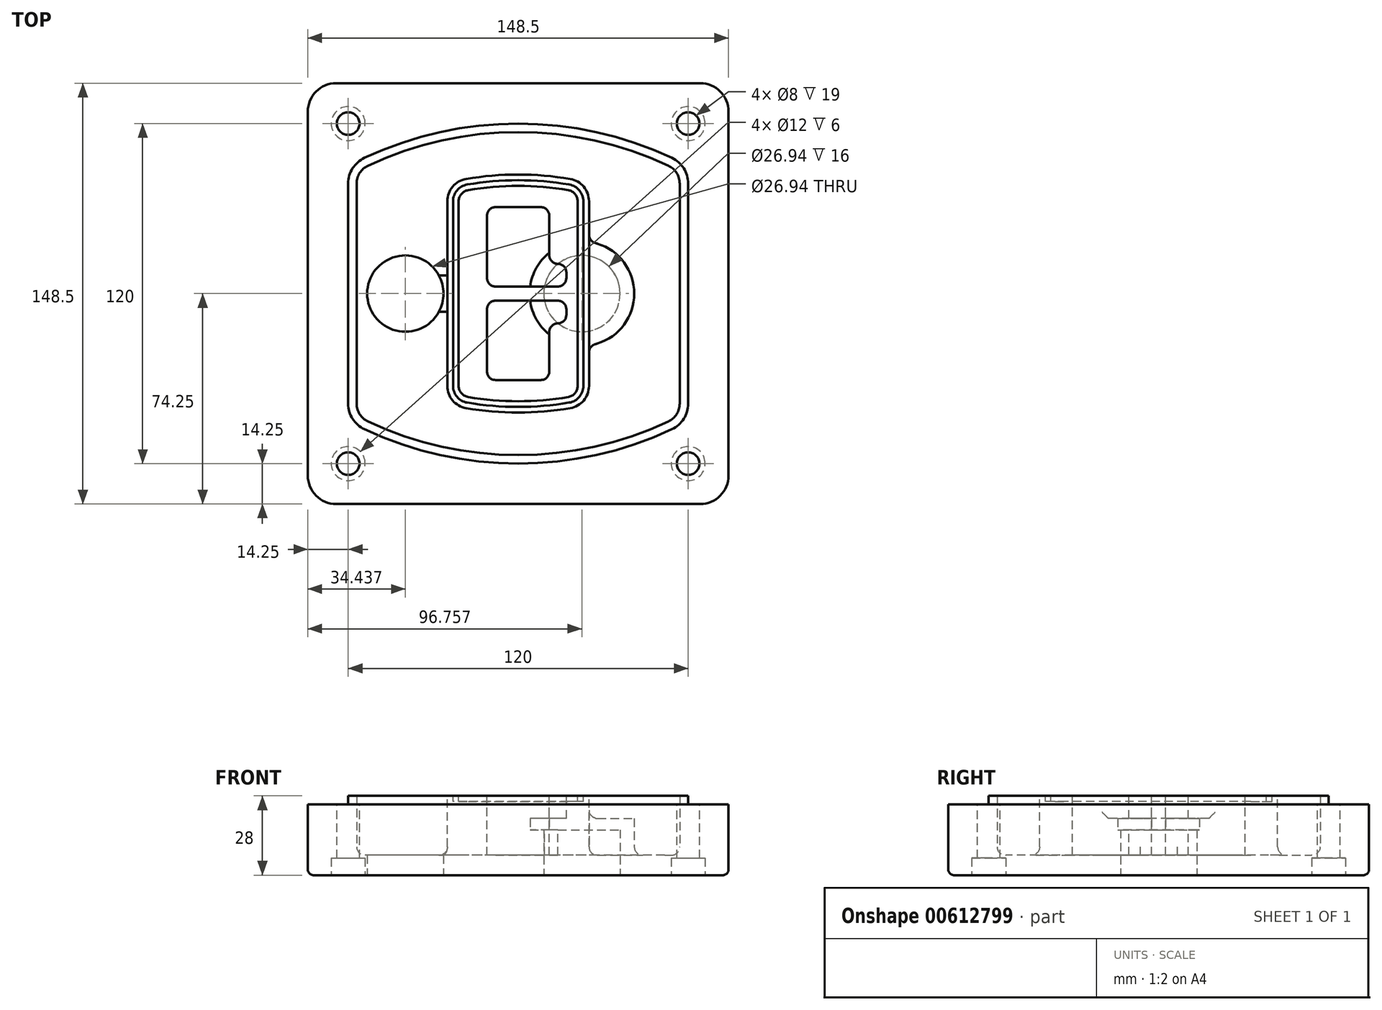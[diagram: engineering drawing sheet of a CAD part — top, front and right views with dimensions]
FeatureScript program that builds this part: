
annotation { "Feature Type Name" : "Feature", "Feature Type Description" : "" }
export const myFeature = defineFeature(function(context is Context, id is Id, definition is map)
    precondition{}
    {
        {
            var Q0;
            Q0=qCreatedBy(makeId("Top.planeOp"),FACE);
            var sketch = newSketch(context, id + "F0", { "sketchPlane" : qUnion([Q0])});
            skPoint(sketch, "E0.rect.middle", {"position": v(0, 0) * mm});
            skLineSegment(sketch, "E1.bottom", {"start": v(-64.25, -74.25) * mm, "end": v(64.25, -74.25) * mm});
            skLineSegment(sketch, "E1.top", {"start": v(-64.25, 74.25) * mm, "end": v(64.25, 74.25) * mm});
            skLineSegment(sketch, "E1.left", {"start": v(-74.25, -64.25) * mm, "end": v(-74.25, 64.25) * mm});
            skLineSegment(sketch, "E1.right", {"start": v(74.25, -64.25) * mm, "end": v(74.25, 64.25) * mm});
            skLineSegment(sketch, "E2", {"start": v(-74.25, 74.25) * mm, "end": v(74.25, -74.25) * mm, "construction": true});
            skLineSegment(sketch, "E3", {"start": v(74.25, 74.25) * mm, "end": v(-74.25, -74.25) * mm, "construction": true});
            skCircle(sketch, "E4", {"center": v(-60, 60) * mm, "radius": 4 * mm});
            skCircle(sketch, "E5", {"center": v(60, 60) * mm, "radius": 4 * mm});
            skCircle(sketch, "E6", {"center": v(60, -60) * mm, "radius": 4 * mm});
            skCircle(sketch, "E7", {"center": v(-60, -60) * mm, "radius": 4 * mm});
            skLineSegment(sketch, "E8", {"start": v(-60, 60) * mm, "end": v(60, 60) * mm, "construction": true});
            skLineSegment(sketch, "E9", {"start": v(60, 60) * mm, "end": v(60, -60) * mm, "construction": true});
            skLineSegment(sketch, "E10", {"start": v(60, -60) * mm, "end": v(-60, -60) * mm, "construction": true});
            skLineSegment(sketch, "E11", {"start": v(-60, -60) * mm, "end": v(-60, 60) * mm, "construction": true});
            skLineSegment(sketch, "E12", {"start": v(-60, 38.83) * mm, "end": v(-60, -38.83) * mm});
            skLineSegment(sketch, "E13", {"start": v(60, 38.83) * mm, "end": v(60, -38.83) * mm});
            skArc(sketch, "E14", {"start": v(54.26, 47.88) * mm, "mid": v(0, 60) * mm, "end": v(-54.26, 47.88) * mm});
            skArc(sketch, "E15", {"start": v(-54.26, -47.88) * mm, "mid": v(0, -60) * mm, "end": v(54.26, -47.88) * mm});
            skLineSegment(sketch, "E16", {"start": v(-60, 0) * mm, "end": v(60, 0) * mm, "construction": true});
            skPoint(sketch, "E17.visualSharp", {"position": v(-60, -45) * mm});
            skArc(sketch, "E17.filletArc", {"start": v(-60, -38.83) * mm, "mid": v(-58.44, -44.2) * mm, "end": v(-54.26, -47.88) * mm});
            skPoint(sketch, "E18.visualSharp", {"position": v(-60, 45) * mm});
            skArc(sketch, "E18.filletArc", {"start": v(-54.26, 47.88) * mm, "mid": v(-58.44, 44.2) * mm, "end": v(-60, 38.83) * mm});
            skPoint(sketch, "E19.visualSharp", {"position": v(60, 45) * mm});
            skArc(sketch, "E19.filletArc", {"start": v(60, 38.83) * mm, "mid": v(58.44, 44.2) * mm, "end": v(54.26, 47.88) * mm});
            skPoint(sketch, "E20.visualSharp", {"position": v(60, -45) * mm});
            skArc(sketch, "E20.filletArc", {"start": v(54.26, -47.88) * mm, "mid": v(58.44, -44.2) * mm, "end": v(60, -38.83) * mm});
            skPoint(sketch, "E21.visualSharp", {"position": v(-74.25, 74.25) * mm});
            skArc(sketch, "E21.filletArc", {"start": v(-64.25, 74.25) * mm, "mid": v(-71.32, 71.32) * mm, "end": v(-74.25, 64.25) * mm});
            skPoint(sketch, "E22.visualSharp", {"position": v(74.25, 74.25) * mm});
            skArc(sketch, "E22.filletArc", {"start": v(74.25, 64.25) * mm, "mid": v(71.32, 71.32) * mm, "end": v(64.25, 74.25) * mm});
            skPoint(sketch, "E23.visualSharp", {"position": v(74.25, -74.25) * mm});
            skArc(sketch, "E23.filletArc", {"start": v(64.25, -74.25) * mm, "mid": v(71.32, -71.32) * mm, "end": v(74.25, -64.25) * mm});
            skPoint(sketch, "E24.visualSharp", {"position": v(-74.25, -74.25) * mm});
            skArc(sketch, "E24.filletArc", {"start": v(-74.25, -64.25) * mm, "mid": v(-71.32, -71.32) * mm, "end": v(-64.25, -74.25) * mm});
            skArc(sketch, "E25.0", {"start": v(57, 38.83) * mm, "mid": v(55.9, 42.58) * mm, "end": v(52.98, 45.17) * mm});
            skLineSegment(sketch, "E25.1", {"start": v(57, 38.83) * mm, "end": v(57, -38.83) * mm});
            skArc(sketch, "E25.2", {"start": v(52.98, -45.17) * mm, "mid": v(55.9, -42.58) * mm, "end": v(57, -38.83) * mm});
            skArc(sketch, "E25.3", {"start": v(-52.98, -45.17) * mm, "mid": v(0, -57) * mm, "end": v(52.98, -45.17) * mm});
            skArc(sketch, "E25.4", {"start": v(-57, -38.83) * mm, "mid": v(-55.9, -42.58) * mm, "end": v(-52.98, -45.17) * mm});
            skArc(sketch, "E25.5", {"start": v(52.98, 45.17) * mm, "mid": v(0, 57) * mm, "end": v(-52.98, 45.17) * mm});
            skLineSegment(sketch, "E25.6", {"start": v(-57, 38.83) * mm, "end": v(-57, -38.83) * mm});
            skArc(sketch, "E25.7", {"start": v(-52.98, 45.17) * mm, "mid": v(-55.9, 42.58) * mm, "end": v(-57, 38.83) * mm});
            skArc(sketch, "E26.0", {"start": v(-55.96, 51.5) * mm, "mid": v(-61.82, 46.33) * mm, "end": v(-64, 38.83) * mm});
            skArc(sketch, "E26.1", {"start": v(55.96, 51.5) * mm, "mid": v(0, 64) * mm, "end": v(-55.96, 51.5) * mm});
            skArc(sketch, "E26.2", {"start": v(64, 38.83) * mm, "mid": v(61.82, 46.33) * mm, "end": v(55.96, 51.5) * mm});
            skLineSegment(sketch, "E26.3", {"start": v(64, 38.83) * mm, "end": v(64, -38.83) * mm});
            skArc(sketch, "E26.4", {"start": v(55.96, -51.5) * mm, "mid": v(61.82, -46.33) * mm, "end": v(64, -38.83) * mm});
            skLineSegment(sketch, "E26.5", {"start": v(-64, 38.83) * mm, "end": v(-64, -38.83) * mm});
            skArc(sketch, "E26.6", {"start": v(-55.96, -51.5) * mm, "mid": v(0, -64) * mm, "end": v(55.96, -51.5) * mm});
            skArc(sketch, "E26.7", {"start": v(-64, -38.83) * mm, "mid": v(-61.82, -46.33) * mm, "end": v(-55.96, -51.5) * mm});
            skSolve(sketch);
        }
        {
            var Q0;
            Q0=makeQuery(id+"F0.imprint","IMPRINT",FACE,{"disambiguationData":[TD([[makeQuery(id+"F0.imprint","IMPRINT",EDGE,{"derivedFrom":sQuery(id+"F0.wireOp",EDGE,"E1.bottom")}),1.0]])]});
            var Q1;
            Q1=makeQuery(id+"F0.imprint","IMPRINT",FACE,{"disambiguationData":[TD([[makeQuery(id+"F0.imprint","IMPRINT",EDGE,{"derivedFrom":sQuery(id+"F0.wireOp",EDGE,"E12")}),1.0]])]});
            var Q2;
            Q2=makeQuery(id+"F0.imprint","IMPRINT",FACE,{"disambiguationData":[TD([[makeQuery(id+"F0.imprint","IMPRINT",EDGE,{"derivedFrom":sQuery(id+"F0.wireOp",EDGE,"E25.0")}),1.0]])]});
            var Q3;
            Q3=makeQuery(id+"F0.imprint","IMPRINT",FACE,{"disambiguationData":[TD([[makeQuery(id+"F0.imprint","IMPRINT",EDGE,{"derivedFrom":sQuery(id+"F0.wireOp",EDGE,"E12")}),-1.0]])]});
            extrude(context, id + "F1", {"entities" : qUnion([Q0, Q1, Q2, Q3]), "oppositeDirection" : true, "depth" : 25 * mm});
        }
        {
            var Q0;
            Q0=makeQuery(id+"F0.imprint","IMPRINT",FACE,{"disambiguationData":[TD([[makeQuery(id+"F0.imprint","IMPRINT",EDGE,{"derivedFrom":sQuery(id+"F0.wireOp",EDGE,"E12")}),1.0]])]});
            extrude(context, id + "F2", {"entities" : qUnion([Q0]), "operationType" : NewBodyOperationType.ADD, "depth" : 3 * mm});
        }
        {
            var Q0;
            Q0=makeQuery(id+"F0.imprint","IMPRINT",FACE,{"disambiguationData":[TD([[makeQuery(id+"F0.imprint","IMPRINT",EDGE,{"derivedFrom":sQuery(id+"F0.wireOp",EDGE,"E25.0")}),1.0]])]});
            extrude(context, id + "F3", {"entities" : qUnion([Q0]), "operationType" : NewBodyOperationType.REMOVE, "oppositeDirection" : true, "depth" : 18 * mm, "offsetDistance" : 25 * mm});
        }
        {
            var Q0;
            Q0=makeQuery(id+"F2.opExtrude","CAP_FACE",FACE,{"disambiguationData":[OSD([sQuery(id+"F0.wireOp",EDGE,"E12"),sQuery(id+"F0.wireOp",EDGE,"E13"),sQuery(id+"F0.wireOp",EDGE,"E14"),sQuery(id+"F0.wireOp",EDGE,"E15"),sQuery(id+"F0.wireOp",EDGE,"E17.filletArc"),sQuery(id+"F0.wireOp",EDGE,"E18.filletArc"),sQuery(id+"F0.wireOp",EDGE,"E19.filletArc"),sQuery(id+"F0.wireOp",EDGE,"E20.filletArc"),sQuery(id+"F0.wireOp",EDGE,"E25.0"),sQuery(id+"F0.wireOp",EDGE,"E25.1"),sQuery(id+"F0.wireOp",EDGE,"E25.2"),sQuery(id+"F0.wireOp",EDGE,"E25.3"),sQuery(id+"F0.wireOp",EDGE,"E25.4"),sQuery(id+"F0.wireOp",EDGE,"E25.5"),sQuery(id+"F0.wireOp",EDGE,"E25.6"),sQuery(id+"F0.wireOp",EDGE,"E25.7")])],"isStart":false});
            var sketch = newSketch(context, id + "F4", { "sketchPlane" : qUnion([Q0])});
            skArc(sketch, "E27.0", {"start": v(-18.34, -40.45) * mm, "mid": v(0, -42) * mm, "end": v(18.34, -40.45) * mm});
            skArc(sketch, "E28.0", {"start": v(18.34, 40.45) * mm, "mid": v(0, 42) * mm, "end": v(-18.34, 40.45) * mm});
            skLineSegment(sketch, "E29", {"start": v(-25, 32.57) * mm, "end": v(-25, -32.57) * mm});
            skLineSegment(sketch, "E30", {"start": v(25, 32.57) * mm, "end": v(25, -32.57) * mm});
            skLineSegment(sketch, "E31", {"start": v(-25, 39.1) * mm, "end": v(25, 39.1) * mm, "construction": true});
            skLineSegment(sketch, "E32", {"start": v(-25, -39.1) * mm, "end": v(25, -39.1) * mm, "construction": true});
            skPoint(sketch, "E33.visualSharp", {"position": v(-25, 39.1) * mm});
            skArc(sketch, "E33.filletArc", {"start": v(-18.34, 40.45) * mm, "mid": v(-23.11, 37.73) * mm, "end": v(-25, 32.57) * mm});
            skPoint(sketch, "E34.visualSharp", {"position": v(25, 39.1) * mm});
            skArc(sketch, "E34.filletArc", {"start": v(25, 32.57) * mm, "mid": v(23.11, 37.73) * mm, "end": v(18.34, 40.45) * mm});
            skPoint(sketch, "E35.visualSharp", {"position": v(25, -39.1) * mm});
            skArc(sketch, "E35.filletArc", {"start": v(18.34, -40.45) * mm, "mid": v(23.11, -37.73) * mm, "end": v(25, -32.57) * mm});
            skPoint(sketch, "E36.visualSharp", {"position": v(-25, -39.1) * mm});
            skArc(sketch, "E36.filletArc", {"start": v(-25, -32.57) * mm, "mid": v(-23.11, -37.73) * mm, "end": v(-18.34, -40.45) * mm});
            skArc(sketch, "E37.0", {"start": v(52.98, 45.17) * mm, "mid": v(0, 57) * mm, "end": v(-52.98, 45.17) * mm});
            skArc(sketch, "E37.1", {"start": v(-52.98, 45.17) * mm, "mid": v(-55.9, 42.58) * mm, "end": v(-57, 38.83) * mm});
            skLineSegment(sketch, "E37.2", {"start": v(-57, 38.83) * mm, "end": v(-57, -38.83) * mm});
            skArc(sketch, "E37.3", {"start": v(-57, -38.83) * mm, "mid": v(-55.9, -42.58) * mm, "end": v(-52.98, -45.17) * mm});
            skArc(sketch, "E37.4", {"start": v(-52.98, -45.17) * mm, "mid": v(0, -57) * mm, "end": v(52.98, -45.17) * mm});
            skArc(sketch, "E37.5", {"start": v(52.98, -45.17) * mm, "mid": v(55.9, -42.58) * mm, "end": v(57, -38.83) * mm});
            skLineSegment(sketch, "E37.6", {"start": v(57, 38.83) * mm, "end": v(57, -38.83) * mm});
            skArc(sketch, "E37.7", {"start": v(57, 38.83) * mm, "mid": v(55.9, 42.58) * mm, "end": v(52.98, 45.17) * mm});
            skLineSegment(sketch, "E38.0", {"start": v(23, 32.57) * mm, "end": v(23, -32.57) * mm});
            skArc(sketch, "E38.1", {"start": v(18, -38.48) * mm, "mid": v(21.58, -36.44) * mm, "end": v(23, -32.57) * mm});
            skArc(sketch, "E38.2", {"start": v(-18, -38.48) * mm, "mid": v(0, -40) * mm, "end": v(18, -38.48) * mm});
            skArc(sketch, "E38.3", {"start": v(-23, -32.57) * mm, "mid": v(-21.58, -36.44) * mm, "end": v(-18, -38.48) * mm});
            skLineSegment(sketch, "E38.4", {"start": v(-23, 32.57) * mm, "end": v(-23, -32.57) * mm});
            skArc(sketch, "E38.5", {"start": v(23, 32.57) * mm, "mid": v(21.58, 36.44) * mm, "end": v(18, 38.48) * mm});
            skArc(sketch, "E38.6", {"start": v(-18, 38.48) * mm, "mid": v(-21.58, 36.44) * mm, "end": v(-23, 32.57) * mm});
            skArc(sketch, "E38.7", {"start": v(18, 38.48) * mm, "mid": v(0, 40) * mm, "end": v(-18, 38.48) * mm});
            skArc(sketch, "E39.0", {"start": v(21, 32.57) * mm, "mid": v(20.06, 35.15) * mm, "end": v(17.67, 36.5) * mm});
            skLineSegment(sketch, "E39.1", {"start": v(21, 32.57) * mm, "end": v(21, -32.57) * mm});
            skArc(sketch, "E39.2", {"start": v(17.67, -36.5) * mm, "mid": v(20.06, -35.15) * mm, "end": v(21, -32.57) * mm});
            skArc(sketch, "E39.3", {"start": v(-17.67, -36.5) * mm, "mid": v(0, -38) * mm, "end": v(17.67, -36.5) * mm});
            skArc(sketch, "E39.4", {"start": v(-21, -32.57) * mm, "mid": v(-20.06, -35.15) * mm, "end": v(-17.67, -36.5) * mm});
            skArc(sketch, "E39.5", {"start": v(17.67, 36.5) * mm, "mid": v(0, 38) * mm, "end": v(-17.67, 36.5) * mm});
            skLineSegment(sketch, "E39.6", {"start": v(-21, 32.57) * mm, "end": v(-21, -32.57) * mm});
            skArc(sketch, "E39.7", {"start": v(-17.67, 36.5) * mm, "mid": v(-20.06, 35.15) * mm, "end": v(-21, 32.57) * mm});
            skLineSegment(sketch, "E40", {"start": v(-25, 0) * mm, "end": v(25, 0) * mm, "construction": true});
            skLineSegment(sketch, "E41", {"start": v(-11, 5.5) * mm, "end": v(-11, 27.5) * mm});
            skLineSegment(sketch, "E42", {"start": v(-8, 30.5) * mm, "end": v(8, 30.5) * mm});
            skLineSegment(sketch, "E43", {"start": v(11, 27.5) * mm, "end": v(11, 13.5) * mm});
            skLineSegment(sketch, "E44", {"start": v(14, 10.5) * mm, "end": v(14, 10.5) * mm});
            skLineSegment(sketch, "E45", {"start": v(17, 7.5) * mm, "end": v(17, 5.5) * mm});
            skLineSegment(sketch, "E46", {"start": v(14, 2.5) * mm, "end": v(-8, 2.5) * mm});
            skPoint(sketch, "E47.visualSharp", {"position": v(-11, 30.5) * mm});
            skArc(sketch, "E47.filletArc", {"start": v(-8, 30.5) * mm, "mid": v(-10.12, 29.62) * mm, "end": v(-11, 27.5) * mm});
            skPoint(sketch, "E48.visualSharp", {"position": v(11, 30.5) * mm});
            skArc(sketch, "E48.filletArc", {"start": v(11, 27.5) * mm, "mid": v(10.12, 29.62) * mm, "end": v(8, 30.5) * mm});
            skPoint(sketch, "E49.visualSharp", {"position": v(11, 10.5) * mm});
            skArc(sketch, "E49.filletArc", {"start": v(11, 13.5) * mm, "mid": v(11.88, 11.38) * mm, "end": v(14, 10.5) * mm});
            skPoint(sketch, "E50.visualSharp", {"position": v(17, 10.5) * mm});
            skArc(sketch, "E50.filletArc", {"start": v(17, 7.5) * mm, "mid": v(16.12, 9.62) * mm, "end": v(14, 10.5) * mm});
            skPoint(sketch, "E51.visualSharp", {"position": v(17, 2.5) * mm});
            skArc(sketch, "E51.filletArc", {"start": v(14, 2.5) * mm, "mid": v(16.12, 3.38) * mm, "end": v(17, 5.5) * mm});
            skPoint(sketch, "E52.visualSharp", {"position": v(-11, 2.5) * mm});
            skArc(sketch, "E52.filletArc", {"start": v(-11, 5.5) * mm, "mid": v(-10.12, 3.38) * mm, "end": v(-8, 2.5) * mm});
            skLineSegment(sketch, "E53.0.MirrorCS", {"start": v(14, -2.5) * mm, "end": v(-8, -2.5) * mm});
            skArc(sketch, "E54.0.MirrorCS", {"start": v(-11, -5.5) * mm, "mid": v(-10.12, -3.38) * mm, "end": v(-8, -2.5) * mm});
            skLineSegment(sketch, "E55.0.MirrorCS", {"start": v(-11, -5.5) * mm, "end": v(-11, -27.5) * mm});
            skArc(sketch, "E56.0.MirrorCS", {"start": v(-8, -30.5) * mm, "mid": v(-10.12, -29.62) * mm, "end": v(-11, -27.5) * mm});
            skLineSegment(sketch, "E57.0.MirrorCS", {"start": v(-8, -30.5) * mm, "end": v(8, -30.5) * mm});
            skArc(sketch, "E58.0.MirrorCS", {"start": v(11, -27.5) * mm, "mid": v(10.12, -29.62) * mm, "end": v(8, -30.5) * mm});
            skLineSegment(sketch, "E59.0.MirrorCS", {"start": v(11, -27.5) * mm, "end": v(11, -13.5) * mm});
            skArc(sketch, "E60.0.MirrorCS", {"start": v(11, -13.5) * mm, "mid": v(11.88, -11.38) * mm, "end": v(14, -10.5) * mm});
            skArc(sketch, "E61.0.MirrorCS", {"start": v(17, -7.5) * mm, "mid": v(16.12, -9.62) * mm, "end": v(14, -10.5) * mm});
            skLineSegment(sketch, "E62.0.MirrorCS", {"start": v(17, -7.5) * mm, "end": v(17, -5.5) * mm});
            skArc(sketch, "E63.0.MirrorCS", {"start": v(14, -2.5) * mm, "mid": v(16.12, -3.38) * mm, "end": v(17, -5.5) * mm});
            skSolve(sketch);
        }
        {
            var Q0;
            Q0=makeQuery(id+"F4.imprint","IMPRINT",FACE,{"disambiguationData":[TD([[makeQuery(id+"F4.imprint","IMPRINT",EDGE,{"derivedFrom":sQuery(id+"F4.wireOp",EDGE,"E27.0")}),1.0]])]});
            var Q1;
            Q1=makeQuery(id+"F4.imprint","IMPRINT",FACE,{"disambiguationData":[TD([[makeQuery(id+"F4.imprint","IMPRINT",EDGE,{"derivedFrom":sQuery(id+"F4.wireOp",EDGE,"E38.0")}),-1.0]])]});
            var Q2;
            Q2=makeQuery(id+"F4.imprint","IMPRINT",FACE,{"disambiguationData":[TD([[makeQuery(id+"F4.imprint","IMPRINT",EDGE,{"derivedFrom":sQuery(id+"F4.wireOp",EDGE,"E39.0")}),1.0]])]});
            extrude(context, id + "F5", {"entities" : qUnion([Q0, Q1, Q2]), "operationType" : NewBodyOperationType.ADD, "endBound" : BoundingType.UP_TO_NEXT, "oppositeDirection" : true, "depth" : 25 * mm});
        }
        {
            var Q0;
            Q0=makeQuery(id+"F4.imprint","IMPRINT",FACE,{"disambiguationData":[TD([[makeQuery(id+"F4.imprint","IMPRINT",EDGE,{"derivedFrom":sQuery(id+"F4.wireOp",EDGE,"E38.0")}),-1.0]])]});
            extrude(context, id + "F6", {"entities" : qUnion([Q0]), "operationType" : NewBodyOperationType.REMOVE, "oppositeDirection" : true, "depth" : 2 * mm});
        }
        {
            var Q0;
            Q0=makeQuery(id+"F1.opExtrude","CAP_FACE",FACE,{"disambiguationData":[OSD([sQuery(id+"F0.wireOp",EDGE,"E1.bottom"),sQuery(id+"F0.wireOp",EDGE,"E1.top"),sQuery(id+"F0.wireOp",EDGE,"E1.left"),sQuery(id+"F0.wireOp",EDGE,"E1.right"),sQuery(id+"F0.wireOp",EDGE,"E4"),sQuery(id+"F0.wireOp",EDGE,"E5"),sQuery(id+"F0.wireOp",EDGE,"E6"),sQuery(id+"F0.wireOp",EDGE,"E7"),sQuery(id+"F0.wireOp",EDGE,"E21.filletArc"),sQuery(id+"F0.wireOp",EDGE,"E22.filletArc"),sQuery(id+"F0.wireOp",EDGE,"E23.filletArc"),sQuery(id+"F0.wireOp",EDGE,"E24.filletArc")])],"isStart":false});
            var sketch = newSketch(context, id + "F7", { "sketchPlane" : qUnion([Q0])});
            skCircle(sketch, "E64", {"center": v(22.5, 0) * mm, "radius": 13.47 * mm});
            skCircle(sketch, "E65", {"center": v(-39.81, 0) * mm, "radius": 13.47 * mm});
            skLineSegment(sketch, "E66", {"start": v(74.25, 0) * mm, "end": v(-74.25, 0) * mm});
            skCircle(sketch, "E67", {"center": v(22.5, 0) * mm, "radius": 18.47 * mm});
            skCircle(sketch, "E68", {"center": v(60, -60) * mm, "radius": 6 * mm});
            skCircle(sketch, "E69", {"center": v(-60, -60) * mm, "radius": 6 * mm});
            skCircle(sketch, "E70", {"center": v(-60, 60) * mm, "radius": 6 * mm});
            skCircle(sketch, "E71", {"center": v(60, 60) * mm, "radius": 6 * mm});
            skSolve(sketch);
        }
        {
            var Q0;
            {var subQ1=sQuery(id+"F7.wireOp",EDGE,"E66");var subQ4=sQuery(id+"F7.wireOp",EDGE,"E64");var subQ6=makeQuery(id+"F7.imprint","INTERSECT",VERTEX,{"disambiguationData":[OD(0.0)],"derivedFrom":[subQ4,subQ1]});Q0=makeQuery(id+"F7.imprint","IMPRINT",FACE,{"disambiguationData":[TD([[makeQuery(id+"F7.imprint","IMPRINT",EDGE,{"disambiguationData":[TD([[subQ6,-1.0]])],"derivedFrom":subQ4}),-1.0]])]});}
            var Q1;
            {var subQ0=sQuery(id+"F7.wireOp",EDGE,"E66");var subQ1=sQuery(id+"F7.wireOp",EDGE,"E64");var subQ3=makeQuery(id+"F7.imprint","INTERSECT",VERTEX,{"disambiguationData":[OD(0.0)],"derivedFrom":[subQ1,subQ0]});Q1=makeQuery(id+"F7.imprint","IMPRINT",FACE,{"disambiguationData":[TD([[makeQuery(id+"F7.imprint","IMPRINT",EDGE,{"disambiguationData":[TD([[subQ3,-1.0]])],"derivedFrom":subQ1}),1.0]])]});}
            var Q2;
            {var subQ0=sQuery(id+"F7.wireOp",EDGE,"E66");var subQ1=sQuery(id+"F7.wireOp",EDGE,"E64");var subQ3=makeQuery(id+"F7.imprint","INTERSECT",VERTEX,{"disambiguationData":[OD(0.0)],"derivedFrom":[subQ1,subQ0]});Q2=makeQuery(id+"F7.imprint","IMPRINT",FACE,{"disambiguationData":[TD([[makeQuery(id+"F7.imprint","IMPRINT",EDGE,{"disambiguationData":[TD([[subQ3,1.0]])],"derivedFrom":subQ1}),1.0]])]});}
            var Q3;
            {var subQ1=sQuery(id+"F7.wireOp",EDGE,"E66");var subQ4=sQuery(id+"F7.wireOp",EDGE,"E64");var subQ6=makeQuery(id+"F7.imprint","INTERSECT",VERTEX,{"disambiguationData":[OD(0.0)],"derivedFrom":[subQ4,subQ1]});Q3=makeQuery(id+"F7.imprint","IMPRINT",FACE,{"disambiguationData":[TD([[makeQuery(id+"F7.imprint","IMPRINT",EDGE,{"disambiguationData":[TD([[subQ6,1.0]])],"derivedFrom":subQ4}),-1.0]])]});}
            extrude(context, id + "F8", {"entities" : qUnion([Q0, Q1, Q2, Q3]), "operationType" : NewBodyOperationType.ADD, "oppositeDirection" : true, "depth" : 20 * mm});
        }
        {
            var Q0;
            {var subQ0=sQuery(id+"F7.wireOp",EDGE,"E66");var subQ1=sQuery(id+"F7.wireOp",EDGE,"E64");var subQ3=makeQuery(id+"F7.imprint","INTERSECT",VERTEX,{"disambiguationData":[OD(0.0)],"derivedFrom":[subQ1,subQ0]});Q0=makeQuery(id+"F7.imprint","IMPRINT",FACE,{"disambiguationData":[TD([[makeQuery(id+"F7.imprint","IMPRINT",EDGE,{"disambiguationData":[TD([[subQ3,-1.0]])],"derivedFrom":subQ1}),1.0]])]});}
            var Q1;
            {var subQ0=sQuery(id+"F7.wireOp",EDGE,"E66");var subQ1=sQuery(id+"F7.wireOp",EDGE,"E64");var subQ3=makeQuery(id+"F7.imprint","INTERSECT",VERTEX,{"disambiguationData":[OD(0.0)],"derivedFrom":[subQ1,subQ0]});Q1=makeQuery(id+"F7.imprint","IMPRINT",FACE,{"disambiguationData":[TD([[makeQuery(id+"F7.imprint","IMPRINT",EDGE,{"disambiguationData":[TD([[subQ3,1.0]])],"derivedFrom":subQ1}),1.0]])]});}
            extrude(context, id + "F9", {"entities" : qUnion([Q0, Q1]), "operationType" : NewBodyOperationType.REMOVE, "oppositeDirection" : true, "depth" : 16 * mm});
        }
        {
            var Q0;
            {var subQ0=sQuery(id+"F7.wireOp",EDGE,"E66");var subQ1=sQuery(id+"F7.wireOp",EDGE,"E65");var subQ3=makeQuery(id+"F7.imprint","INTERSECT",VERTEX,{"disambiguationData":[OD(0.0)],"derivedFrom":[subQ1,subQ0]});Q0=makeQuery(id+"F7.imprint","IMPRINT",FACE,{"disambiguationData":[TD([[makeQuery(id+"F7.imprint","IMPRINT",EDGE,{"disambiguationData":[TD([[subQ3,-1.0]])],"derivedFrom":subQ1}),1.0]])]});}
            var Q1;
            {var subQ0=sQuery(id+"F7.wireOp",EDGE,"E66");var subQ1=sQuery(id+"F7.wireOp",EDGE,"E65");var subQ3=makeQuery(id+"F7.imprint","INTERSECT",VERTEX,{"disambiguationData":[OD(0.0)],"derivedFrom":[subQ1,subQ0]});Q1=makeQuery(id+"F7.imprint","IMPRINT",FACE,{"disambiguationData":[TD([[makeQuery(id+"F7.imprint","IMPRINT",EDGE,{"disambiguationData":[TD([[subQ3,1.0]])],"derivedFrom":subQ1}),1.0]])]});}
            extrude(context, id + "F10", {"entities" : qUnion([Q0, Q1]), "operationType" : NewBodyOperationType.REMOVE, "oppositeDirection" : true, "depth" : 25 * mm});
        }
        {
            var Q0;
            Q0=makeQuery(id+"F7.imprint","IMPRINT",FACE,{"disambiguationData":[TD([[makeQuery(id+"F7.imprint","IMPRINT",EDGE,{"derivedFrom":sQuery(id+"F7.wireOp",EDGE,"E68")}),1.0]])]});
            var Q1;
            Q1=makeQuery(id+"F7.imprint","IMPRINT",FACE,{"disambiguationData":[TD([[makeQuery(id+"F7.imprint","IMPRINT",EDGE,{"derivedFrom":makeQuery(id+"F1.opExtrude","CAP_EDGE",EDGE,{"disambiguationData":[OSD([sQuery(id+"F0.wireOp",EDGE,"E5")])],"isStart":false})}),-1.0]])]});
            var Q2;
            Q2=makeQuery(id+"F7.imprint","IMPRINT",FACE,{"disambiguationData":[TD([[makeQuery(id+"F7.imprint","IMPRINT",EDGE,{"derivedFrom":sQuery(id+"F7.wireOp",EDGE,"E69")}),1.0]])]});
            var Q3;
            Q3=makeQuery(id+"F7.imprint","IMPRINT",FACE,{"disambiguationData":[TD([[makeQuery(id+"F7.imprint","IMPRINT",EDGE,{"derivedFrom":makeQuery(id+"F1.opExtrude","CAP_EDGE",EDGE,{"disambiguationData":[OSD([sQuery(id+"F0.wireOp",EDGE,"E4")])],"isStart":false})}),-1.0]])]});
            var Q4;
            Q4=makeQuery(id+"F7.imprint","IMPRINT",FACE,{"disambiguationData":[TD([[makeQuery(id+"F7.imprint","IMPRINT",EDGE,{"derivedFrom":sQuery(id+"F7.wireOp",EDGE,"E70")}),1.0]])]});
            var Q5;
            Q5=makeQuery(id+"F7.imprint","IMPRINT",FACE,{"disambiguationData":[TD([[makeQuery(id+"F7.imprint","IMPRINT",EDGE,{"derivedFrom":makeQuery(id+"F1.opExtrude","CAP_EDGE",EDGE,{"disambiguationData":[OSD([sQuery(id+"F0.wireOp",EDGE,"E7")])],"isStart":false})}),-1.0]])]});
            var Q6;
            Q6=makeQuery(id+"F7.imprint","IMPRINT",FACE,{"disambiguationData":[TD([[makeQuery(id+"F7.imprint","IMPRINT",EDGE,{"derivedFrom":sQuery(id+"F7.wireOp",EDGE,"E71")}),1.0]])]});
            var Q7;
            Q7=makeQuery(id+"F7.imprint","IMPRINT",FACE,{"disambiguationData":[TD([[makeQuery(id+"F7.imprint","IMPRINT",EDGE,{"derivedFrom":makeQuery(id+"F1.opExtrude","CAP_EDGE",EDGE,{"disambiguationData":[OSD([sQuery(id+"F0.wireOp",EDGE,"E6")])],"isStart":false})}),-1.0]])]});
            extrude(context, id + "F11", {"entities" : qUnion([Q0, Q1, Q2, Q3, Q4, Q5, Q6, Q7]), "operationType" : NewBodyOperationType.REMOVE, "oppositeDirection" : true, "depth" : 6 * mm});
        }
        {
            var Q0;
            Q0=makeQuery(id+"F9.boolean.opBoolean","COPY",FACE,{"derivedFrom":makeQuery(id+"F9.opExtrude","CAP_FACE",FACE,{"disambiguationData":[OSD([sQuery(id+"F7.wireOp",EDGE,"E64")])],"isStart":false})});
            var sketch = newSketch(context, id + "F12", { "sketchPlane" : qUnion([Q0])});
            skArc(sketch, "E72.0", {"start": v(11, 14.45) * mm, "mid": v(6.45, 9.13) * mm, "end": v(4.2, 2.5) * mm});
            skArc(sketch, "E72.1", {"start": v(4.2, -2.5) * mm, "mid": v(6.45, -9.13) * mm, "end": v(11, -14.45) * mm});
            skLineSegment(sketch, "E73", {"start": v(4.2, -2.5) * mm, "end": v(14, -2.5) * mm});
            skLineSegment(sketch, "E74.0", {"start": v(14, 2.5) * mm, "end": v(4.2, 2.5) * mm});
            skArc(sketch, "E74.1", {"start": v(14, 2.5) * mm, "mid": v(16.12, 3.38) * mm, "end": v(17, 5.5) * mm});
            skLineSegment(sketch, "E74.2", {"start": v(17, 7.5) * mm, "end": v(17, 5.5) * mm});
            skArc(sketch, "E74.3", {"start": v(17, 7.5) * mm, "mid": v(16.12, 9.62) * mm, "end": v(14, 10.5) * mm});
            skArc(sketch, "E74.4", {"start": v(11, 13.5) * mm, "mid": v(11.88, 11.38) * mm, "end": v(14, 10.5) * mm});
            skLineSegment(sketch, "E74.5", {"start": v(11, 14.45) * mm, "end": v(11, 13.5) * mm});
            skLineSegment(sketch, "E74.7", {"start": v(14, -2.5) * mm, "end": v(4.2, -2.5) * mm});
            skArc(sketch, "E74.8", {"start": v(14, -2.5) * mm, "mid": v(16.12, -3.38) * mm, "end": v(17, -5.5) * mm});
            skLineSegment(sketch, "E74.9", {"start": v(17, -7.5) * mm, "end": v(17, -5.5) * mm});
            skArc(sketch, "E74.10", {"start": v(17, -7.5) * mm, "mid": v(16.12, -9.62) * mm, "end": v(14, -10.5) * mm});
            skArc(sketch, "E74.11", {"start": v(11, -13.5) * mm, "mid": v(11.88, -11.38) * mm, "end": v(14, -10.5) * mm});
            skLineSegment(sketch, "E74.12", {"start": v(11, -14.45) * mm, "end": v(11, -13.5) * mm});
            skPoint(sketch, "E75.orphan", {"position": v(11, -27.5) * mm});
            skPoint(sketch, "E76.orphan", {"position": v(-8, -2.5) * mm});
            skPoint(sketch, "E77.orphan", {"position": v(-8, 2.5) * mm});
            skPoint(sketch, "E78.orphan", {"position": v(11, 27.5) * mm});
            skSolve(sketch);
        }
        {
            var Q0;
            {var subQ7=sQuery(id+"F12.wireOp",EDGE,"E72.0");var subQ14=sQuery(id+"F12.wireOp",EDGE,"E72.1");var subQ16=sQuery(id+"F12.wireOp",EDGE,"E74.1");var subQ18=sQuery(id+"F12.wireOp",EDGE,"E74.8");Q0=qUnion([makeQuery(id+"F12.imprint","IMPRINT",FACE,{"disambiguationData":[TD([[makeQuery(id+"F12.imprint","IMPRINT",EDGE,{"derivedFrom":subQ7}),1.0]])]}),makeQuery(id+"F12.imprint","IMPRINT",FACE,{"disambiguationData":[TD([[makeQuery(id+"F12.imprint","IMPRINT",EDGE,{"derivedFrom":subQ14}),1.0]])]}),makeQuery(id+"F12.imprint","IMPRINT",FACE,{"disambiguationData":[TD([[makeQuery(id+"F12.imprint","IMPRINT",EDGE,{"derivedFrom":subQ16}),1.0]])]}),makeQuery(id+"F12.imprint","IMPRINT",FACE,{"disambiguationData":[TD([[makeQuery(id+"F12.imprint","IMPRINT",EDGE,{"derivedFrom":subQ18}),-1.0]])]})]);}
            var Q1;
            Q1=makeQuery(id+"F5.boolean.opBoolean","SPLIT",FACE,{"disambiguationData":[TD([makeQuery(id+"F5.opExtrude","SWEPT_FACE",FACE,{"disambiguationData":[OSD([sQuery(id+"F4.wireOp",EDGE,"E41")])]})])],"derivedFrom":makeQuery(id+"F3.boolean.opBoolean","COPY",FACE,{"derivedFrom":makeQuery(id+"F3.opExtrude","CAP_FACE",FACE,{"disambiguationData":[OSD([sQuery(id+"F0.wireOp",EDGE,"E25.0"),sQuery(id+"F0.wireOp",EDGE,"E25.1"),sQuery(id+"F0.wireOp",EDGE,"E25.2"),sQuery(id+"F0.wireOp",EDGE,"E25.3"),sQuery(id+"F0.wireOp",EDGE,"E25.4"),sQuery(id+"F0.wireOp",EDGE,"E25.5"),sQuery(id+"F0.wireOp",EDGE,"E25.6"),sQuery(id+"F0.wireOp",EDGE,"E25.7")])],"isStart":false})})});
            extrude(context, id + "F13", {"entities" : qUnion([Q0]), "operationType" : NewBodyOperationType.REMOVE, "endBound" : BoundingType.UP_TO_SURFACE, "endBoundEntityFace" : qUnion([Q1]), "depth" : 25 * mm});
        }
        {
            var Q0;
            Q0=makeQuery(id+"F3.boolean.opBoolean","COPY",EDGE,{"derivedFrom":makeQuery(id+"F3.opExtrude","CAP_EDGE",EDGE,{"disambiguationData":[OSD([sQuery(id+"F0.wireOp",EDGE,"E25.6")])],"isStart":false})});
            var Q1;
            Q1=makeQuery(id+"F8.boolean.opBoolean","INTERSECT",EDGE,{"derivedFrom":[makeQuery(id+"F5.opExtrude","SWEPT_FACE",FACE,{"disambiguationData":[OSD([sQuery(id+"F4.wireOp",EDGE,"E30")])]}),makeQuery(id+"F8.opExtrude","CAP_FACE",FACE,{"disambiguationData":[OSD([sQuery(id+"F7.wireOp",EDGE,"E67")])],"isStart":false})]});
            var Q2;
            Q2=makeQuery(id+"F8.boolean.opBoolean","INTERSECT",EDGE,{"disambiguationData":[OD(1.0)],"derivedFrom":[makeQuery(id+"F5.opExtrude","SWEPT_FACE",FACE,{"disambiguationData":[OSD([sQuery(id+"F4.wireOp",EDGE,"E30")])]}),makeQuery(id+"F8.opExtrude","SWEPT_FACE",FACE,{"disambiguationData":[OSD([sQuery(id+"F7.wireOp",EDGE,"E67")])]})]});
            var Q3;
            {var subQ0=sQuery(id+"F4.wireOp",EDGE,"E30");Q3=makeQuery(id+"F8.boolean.opBoolean","SPLIT",EDGE,{"disambiguationData":[TD([makeQuery(id+"F5.opExtrude","SWEPT_FACE",FACE,{"disambiguationData":[OSD([sQuery(id+"F4.wireOp",EDGE,"E35.filletArc")])]})])],"derivedFrom":makeQuery(id+"F5.opExtrude","CAP_EDGE",EDGE,{"disambiguationData":[OSD([subQ0])],"isStart":false})});}
            var Q4;
            {var subQ0=sQuery(id+"F0.wireOp",EDGE,"E25.7");var subQ1=sQuery(id+"F0.wireOp",EDGE,"E25.1");var subQ2=sQuery(id+"F0.wireOp",EDGE,"E25.6");var subQ3=sQuery(id+"F0.wireOp",EDGE,"E25.5");var subQ4=sQuery(id+"F0.wireOp",EDGE,"E25.4");var subQ5=sQuery(id+"F0.wireOp",EDGE,"E25.0");var subQ6=sQuery(id+"F0.wireOp",EDGE,"E25.2");var subQ7=sQuery(id+"F0.wireOp",EDGE,"E25.3");Q4=makeQuery(id+"F8.boolean.opBoolean","INTERSECT",EDGE,{"derivedFrom":[makeQuery(id+"F5.boolean.opBoolean","SPLIT",FACE,{"disambiguationData":[TD([makeQuery(id+"F2.opExtrude","SWEPT_FACE",FACE,{"disambiguationData":[OSD([subQ5])]})])],"derivedFrom":makeQuery(id+"F3.boolean.opBoolean","COPY",FACE,{"derivedFrom":makeQuery(id+"F3.opExtrude","CAP_FACE",FACE,{"disambiguationData":[OSD([subQ5,subQ1,subQ6,subQ7,subQ4,subQ3,subQ2,subQ0])],"isStart":false})})}),makeQuery(id+"F8.opExtrude","SWEPT_FACE",FACE,{"disambiguationData":[OSD([sQuery(id+"F7.wireOp",EDGE,"E67")])]})]});}
            var Q5;
            Q5=makeQuery(id+"F8.boolean.opBoolean","INTERSECT",EDGE,{"disambiguationData":[OD(0.0)],"derivedFrom":[makeQuery(id+"F5.opExtrude","SWEPT_FACE",FACE,{"disambiguationData":[OSD([sQuery(id+"F4.wireOp",EDGE,"E30")])]}),makeQuery(id+"F8.opExtrude","SWEPT_FACE",FACE,{"disambiguationData":[OSD([sQuery(id+"F7.wireOp",EDGE,"E67")])]})]});
            fillet(context, id + "F14", {"entities" : qUnion([Q0, Q1, Q2, Q3, Q4, Q5]), "radius" : 3 * mm, "tangentPropagation" : true, "allowEdgeOverflow" : false});
        }
        {
            var Q0;
            Q0=makeQuery(id+"F1.opExtrude","CAP_EDGE",EDGE,{"disambiguationData":[OSD([sQuery(id+"F0.wireOp",EDGE,"E1.bottom")])],"isStart":false});
            fillet(context, id + "F15", {"entities" : qUnion([Q0]), "radius" : 2 * mm, "tangentPropagation" : true, "allowEdgeOverflow" : false});
        }
    });
